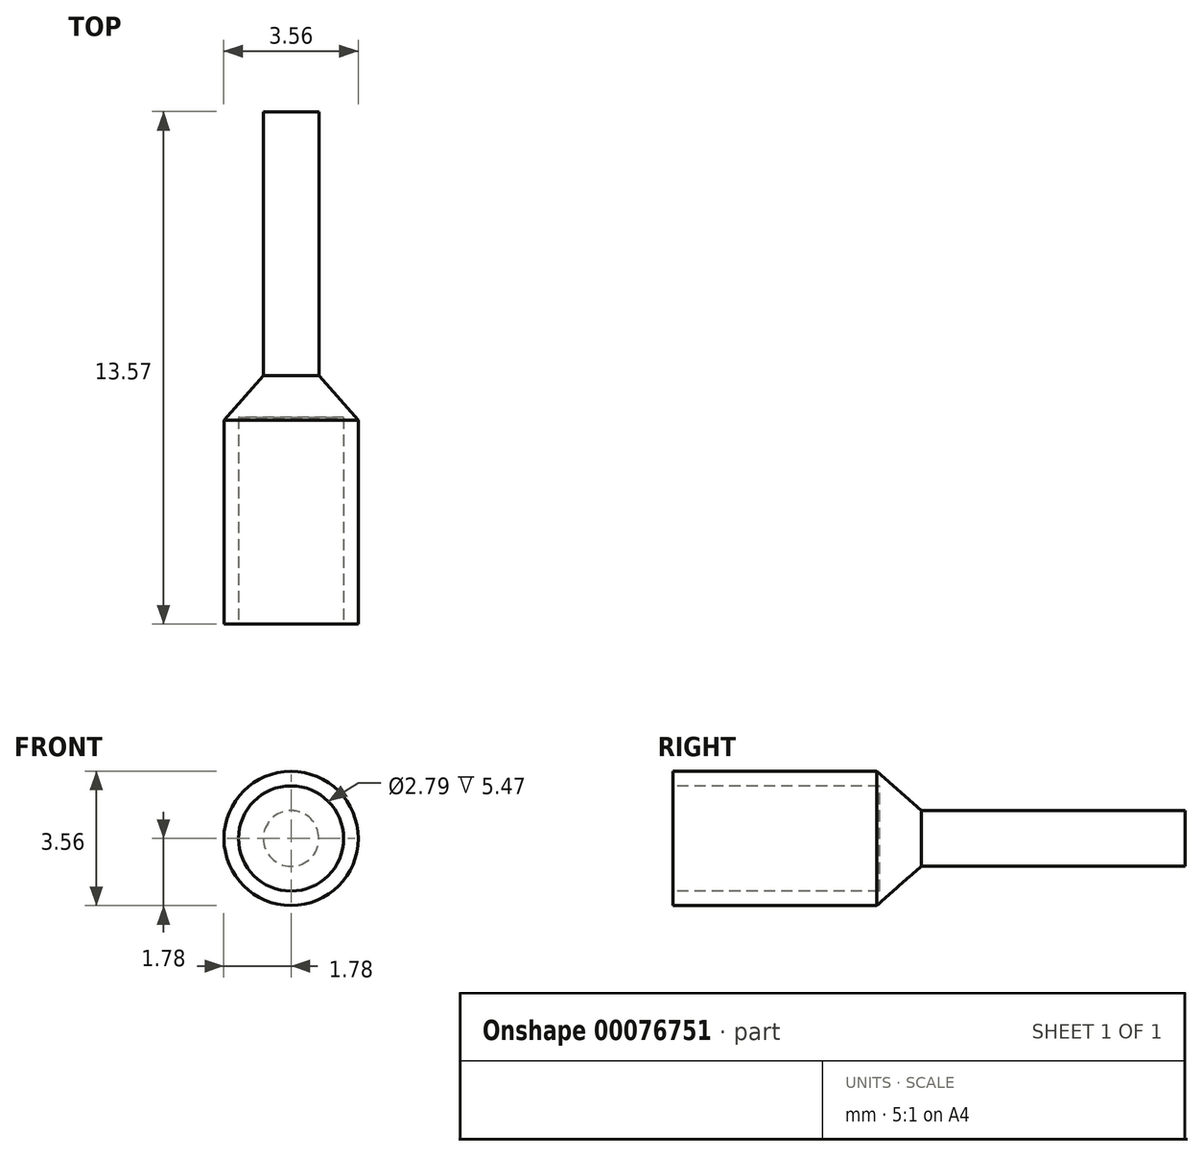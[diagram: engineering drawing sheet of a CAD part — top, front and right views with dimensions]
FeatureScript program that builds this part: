
annotation { "Feature Type Name" : "Feature", "Feature Type Description" : "" }
export const myFeature = defineFeature(function(context is Context, id is Id, definition is map)
    precondition{}
    {
        {
            var Q0;
            Q0=qCreatedBy(makeId("Top.planeOp"),FACE);
            var sketch = newSketch(context, id + "F0", { "sketchPlane" : qUnion([Q0])});
            skLineSegment(sketch, "E0", {"start": v(0, 0) * mm, "end": v(0, 6.58) * mm});
            skLineSegment(sketch, "E1", {"start": v(0, 0) * mm, "end": v(1.78, 0) * mm});
            skLineSegment(sketch, "E2", {"start": v(1.78, 0) * mm, "end": v(1.78, 5.4) * mm});
            skLineSegment(sketch, "E3", {"start": v(0, 6.58) * mm, "end": v(0.74, 6.58) * mm});
            skLineSegment(sketch, "E4", {"start": v(0.74, 6.58) * mm, "end": v(1.78, 5.4) * mm});
            skSolve(sketch);
        }
        {
            var Q0;
            Q0=makeQuery(id+"F0.imprint","IMPRINT",FACE,{"disambiguationData":[TD([[makeQuery(id+"F0.imprint","IMPRINT",EDGE,{"derivedFrom":sQuery(id+"F0.wireOp",EDGE,"E0")}),-1.0]])]});
            var Q1;
            Q1=sQuery(id+"F0.wireOp",EDGE,"E0");
            revolve(context, id + "F1", {"entities" : qUnion([Q0]), "axis" : qUnion([Q1]), "revolveType" : RevolveType.FULL});
        }
        {
            var Q0;
            Q0=qCreatedBy(makeId("Right.planeOp"),FACE);
            var sketch = newSketch(context, id + "F2", { "sketchPlane" : qUnion([Q0])});
            skLineSegment(sketch, "E5", {"start": v(6.58, 0) * mm, "end": v(13.57, 0) * mm});
            skLineSegment(sketch, "E6", {"start": v(13.57, 0) * mm, "end": v(13.57, 0.74) * mm});
            skLineSegment(sketch, "E7", {"start": v(13.57, 0.74) * mm, "end": v(6.57, 0.74) * mm});
            skLineSegment(sketch, "E8", {"start": v(6.57, 0.74) * mm, "end": v(6.58, 0) * mm});
            skSolve(sketch);
        }
        {
            var Q0;
            Q0=makeQuery(id+"F2.imprint","IMPRINT",FACE,{"disambiguationData":[TD([[makeQuery(id+"F2.imprint","IMPRINT",EDGE,{"derivedFrom":sQuery(id+"F2.wireOp",EDGE,"E5")}),1.0]])]});
            var Q1;
            Q1=sQuery(id+"F2.wireOp",EDGE,"E5");
            revolve(context, id + "F3", {"entities" : qUnion([Q0]), "axis" : qUnion([Q1]), "revolveType" : RevolveType.FULL});
        }
        {
            var Q0;
            Q0=makeQuery(id+"F1.opRevolve","SWEPT_FACE",FACE,{"disambiguationData":[OSD([sQuery(id+"F0.wireOp",EDGE,"E1")])]});
            var sketch = newSketch(context, id + "F4", { "sketchPlane" : qUnion([Q0])});
            skCircle(sketch, "E9", {"center": v(0, 0) * mm, "radius": 1.4 * mm});
            skSolve(sketch);
        }
        {
            var Q0;
            Q0=makeQuery(id+"F4.imprint","IMPRINT",FACE,{"disambiguationData":[TD([[makeQuery(id+"F4.imprint","IMPRINT",EDGE,{"derivedFrom":sQuery(id+"F4.wireOp",EDGE,"E9")}),1.0]])]});
            extrude(context, id + "F5", {"entities" : qUnion([Q0]), "operationType" : NewBodyOperationType.REMOVE, "oppositeDirection" : true, "depth" : 5.47 * mm});
        }
    });
